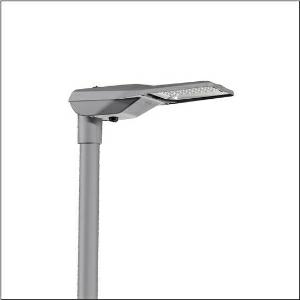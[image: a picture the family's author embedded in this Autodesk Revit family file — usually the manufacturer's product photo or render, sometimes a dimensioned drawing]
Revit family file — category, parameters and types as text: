
# Revit family: streetlight_sl_21_mini___st1_0a_5xe2d33t08jb_5341
name_source: partatom
category: Lighting Fixtures
units: mm (PartAtom-declared; Revit-internal decimal feet)

## family parameters
Cut with Voids When Loaded = No
Host = Face
Light Source = No
Part Type = Normal
Room Calculation Point = No
Round Connector Dimension = Use Diameter
Shared = No

## types (1)
- --- (1 x LED, 12940 lm, 88.6 W, 3000K)
    Apparent Load = 89 VA
    CIE Flux Codes = 40 73 97 100 100
    Color Rendering = 70
    Color Temperature = 3000K
    Default Elevation = 1800 mm
    Description = Streetlight SL 21 mini, mast luminaire, primary light control with lens, of PMMA, primary optical cover: cover, of toughened safety glass, transparent, light distribution: ST1.0a, light emission: direct distribution, primary light characteristic: asymmetric, installation type: side-entry, post-top, LED, High Power LED, rated luminous flux: 12.940lm, luminous efficacy: 146lm/W, light colour: 730, colour temperature: 3000K, control gear: D4i, control: flexible luminous flux parameterisation, time-dependent luminous flux control, constant luminous flux control, overheat protection, pre-setting: logarithmic dimming characteristic, mains connection: 220..240V, AC, 50/60Hz, start of lifetime: 89W, end of service life: 92W, reduction: 41W, luminaire housing, of diecast aluminium, powder-coated, Siteco® metallic grey (DB 702S), corrosivity category C5 mid according to DIN EN ISO 12944, please order mast flange separately, inclination adjustable: 0°, 5°, 10°, 15°, sealing non-destructively replaceable, multi-level sealing system, length: 628mm, width: 235mm, height: 110mm, mast flange for spigot size: 42mm (side-entry): 5XC10008XM4, 60/48mm (side-entry/post-top): 5XC10108XM2, 76/60mm (side-entry/post-top): 5XC10108XM1, mounting height: 4..8m, Smart Interface below and above, protection rating (complete): IP66, insulation class (complete): insulation class II (safety insulation), certification: CE, ENEC, ENEC+, VDE, impact resistance: IK10, permissible operating ambient temperature for outdoor applications: -40..+50°C, standard-compliant lighting for roads and squares, packaging unit: 1 piece

Light Distribution: ST1.0a
    Height = 110 mm
    Lamp = 1 x LED
    Lamp Light Flux = 12940 lm
    Lamp Power = 88.6 W
    Lamp count = 1
    Length = 625 mm
    Luminous efficacy = 146 lm/W
    Manufacturer = Siteco
    ModVariant = No
    Model = 5XE2D33T08JB
    Number of Poles = 1
    OnlyDefault = Yes
    Power Factor = 1
    Product Name = Streetlight SL 21 mini | ST1.0a
    Product group = mast luminaire | pylon top
    ProductGroupID = 6100
    Protection Class = Protection class II
    Protection Degree = IP 66
    RLX_Detail_Level = 1
    RLX_Emergency_Light_Flux = 0 lm
    RLX_Emergency_Type = 0
    RLX_Emergency_Type_DB = No
    RlxData = <blob elided: 26433 chars, md5=7c9e3e61>
    Socket = socket
    Standby Power = 0 W
    System Light Flux = 12940 lm
    System Power = 89 W
    Type Comments = factory setting: luminous flux: 100 % | dim-lin: 254 | 915 mA
    Type Image = l_1003514.jpg
    URL = http://relux.com
    VarID = @adj_011643
    Voltage = 0 V
    Weight = 0.00 kg
    Width = 234 mm

## geometry (parser evidence)
native form markers: Blend x4, Sweep x12
no freeform markers — native parametric forms only
